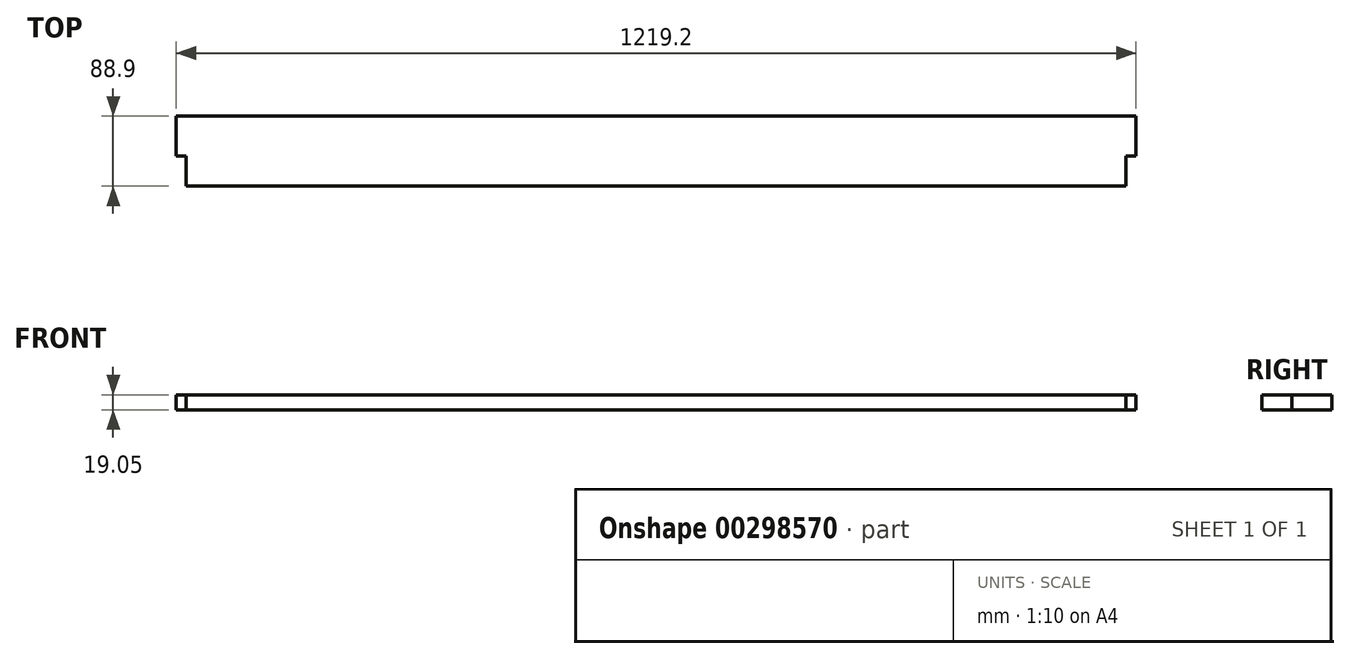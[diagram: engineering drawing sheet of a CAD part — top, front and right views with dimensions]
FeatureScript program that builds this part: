
annotation { "Feature Type Name" : "Feature", "Feature Type Description" : "" }
export const myFeature = defineFeature(function(context is Context, id is Id, definition is map)
    precondition{}
    {
        {
            assignVariable(context, id + "F0", {"name" : "thickness", "anyValue" : 19.05 * mm});
        }
        {
            var Q0;
            Q0=qCreatedBy(makeId("Top.planeOp"),FACE);
            var sketch = newSketch(context, id + "F1", { "sketchPlane" : qUnion([Q0])});
            skLineSegment(sketch, "E0.bottom", {"start": v(-596.9, 0) * mm, "end": v(0, 0) * mm});
            skLineSegment(sketch, "E0.top", {"start": v(-609.6, 88.9) * mm, "end": v(0, 88.9) * mm});
            skLineSegment(sketch, "E0.left", {"start": v(-609.6, 38.1) * mm, "end": v(-609.6, 88.9) * mm});
            skLineSegment(sketch, "E0.right", {"start": v(0, 0) * mm, "end": v(0, 88.9) * mm});
            skLineSegment(sketch, "E1", {"start": v(-609.6, 38.1) * mm, "end": v(-596.9, 38.1) * mm});
            skLineSegment(sketch, "E2", {"start": v(-596.9, 38.1) * mm, "end": v(-596.9, 0) * mm});
            skPoint(sketch, "E3.orphan", {"position": v(-609.6, 0) * mm});
            skSolve(sketch);
        }
        {
            var Q0;
            Q0 = qSketchRegion(id + "F1", true);
            extrude(context, id + "F2", {"entities" : qUnion([Q0]), "depth" : getVariable(context, 'thickness')});
        }
        {
            var Q0;
            Q0=makeQuery(id+"F2.opExtrude","SWEPT_BODY",BODY,{"disambiguationData":[OSD([sQuery(id+"F1.wireOp",EDGE,"E0.bottom"),sQuery(id+"F1.wireOp",EDGE,"E0.top"),sQuery(id+"F1.wireOp",EDGE,"E0.left"),sQuery(id+"F1.wireOp",EDGE,"E0.right"),sQuery(id+"F1.wireOp",EDGE,"ugzCx68c-ccqS-NMhf-mNX6-PG5tSojUVizz"),sQuery(id+"F1.wireOp",EDGE,"lvGux8d6-YpEJ-ahQn-mCon-WTiV8fQDGcFm"),sQuery(id+"F1.wireOp",EDGE,"U01dfa86-yZj2-FbV8-UQFM-C4FsWVFJWgNd")])]});
            var Q1;
            Q1=qCreatedBy(makeId("Right.planeOp"),FACE);
            mirror(context, id + "F3", {"operationType" : NewBodyOperationType.ADD, "entities" : qUnion([Q0]), "mirrorPlane" : qUnion([Q1])});
        }
    });
